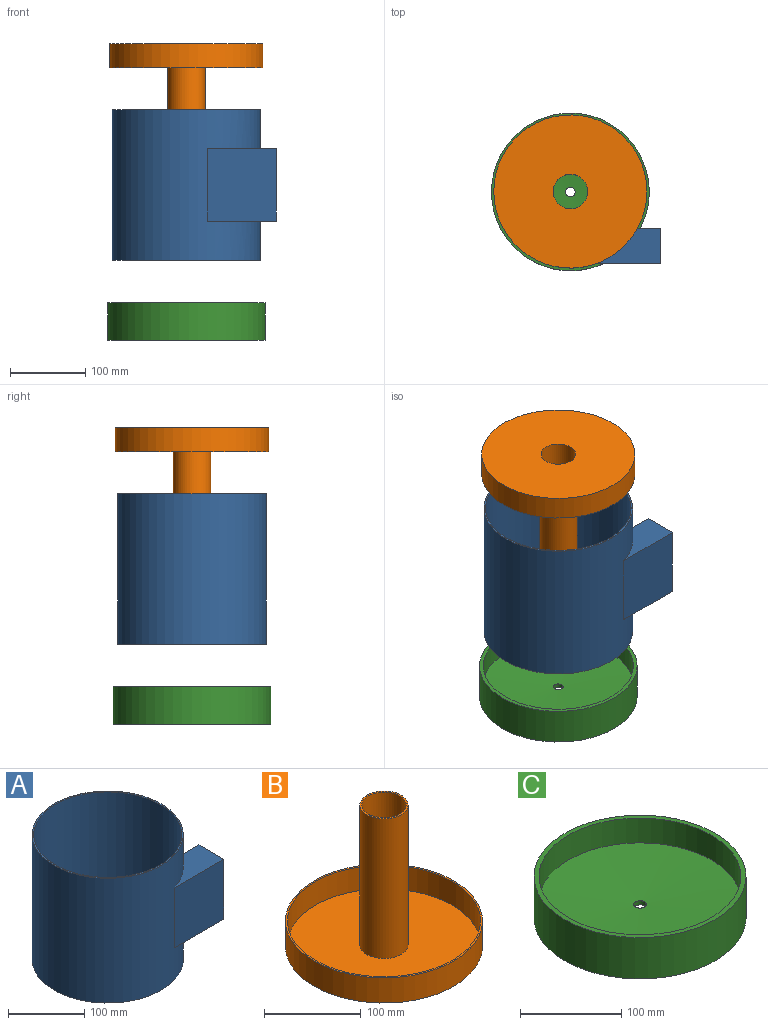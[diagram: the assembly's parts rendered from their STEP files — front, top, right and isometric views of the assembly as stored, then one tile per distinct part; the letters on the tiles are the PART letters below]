
ASSEMBLY  parts=3 mates=3
PART A: 9 faces, bbox 219x198x200 mm
  f0: cylinder r=99mm len=200mm, axis (0,0,-1), area 117110mm2, adj f2,f3,f4,f5,f6,f7
  f1: cylinder r=97mm len=200mm, axis (0,0,-1), area 121893.8mm2, adj f2,f3
  f2: plane 198x198mm, normal (0,0,-1), area 1231.5mm2, adj f0,f1
  f3: plane 198x198mm, normal (0,0,1), area 1231.5mm2, adj f0,f1
  f4: plane 96x92.14mm, normal (0,-1,0), area 8845.7mm2, adj f0,f5,f6,f8
  f5: plane 92.14x46mm, normal (0,0,1), area 2541.8mm2, adj f0,f4,f7,f8
  f6: plane 92.14x46mm, normal (0,0,-1), area 2541.8mm2, adj f0,f4,f7,f8
  f7: plane 96x33.98mm, normal (0,1,0), area 3261.8mm2, adj f0,f5,f6,f8
  f8: plane 96x46mm, normal (1,0,0), area 4416mm2, adj f4,f5,f6,f7
PART B: 8 faces, bbox 204x204x179 mm
  f0: cylinder r=102mm len=204mm, axis (0,0,-1), area 20508.3mm2, adj f1,f7
  f1: plane 204x204mm, normal (0,0,-1), area 31023.2mm2, adj f0,f2
  f2: cylinder r=23mm len=179mm, axis (0,0,-1), area 25867.9mm2, adj f1,f3
  f3: plane 50x50mm, normal (0,0,1), area 301.6mm2, adj f2,f4
  f4: cylinder r=25mm len=177mm, axis (0,0,-1), area 27803.1mm2, adj f3,f5
  f5: plane 200x200mm, normal (0,0,1), area 29452.4mm2, adj f4,f6
  f6: cylinder r=100mm len=200mm, axis (0,0,-1), area 18849.6mm2, adj f5,f7
  f7: plane 204x204mm, normal (0,0,1), area 1269.2mm2, adj f0,f6
PART C: 8 faces, bbox 210x210x50 mm
  f0: cylinder r=100mm len=200mm, axis (0,0,-1), area 9421.9mm2, adj f1,f7
  f1: cone r=6.35mm half-angle=87.6deg, axis (0,0,1), area 31317.8mm2, adj f0,f2
  f2: cylinder r=6.35mm len=12.7mm, axis (0,0,-1), area 199.7mm2, adj f1,f3
  f3: cone r=6.35mm half-angle=87.6deg, axis (0,0,1), area 31317.8mm2, adj f2,f4
  f4: cylinder r=100mm len=200mm, axis (0,0,-1), area 18849.6mm2, adj f3,f5
  f5: plane 210x210mm, normal (0,0,1), area 3220.1mm2, adj f4,f6
  f6: cylinder r=105mm len=210mm, axis (0,0,-1), area 32986.7mm2, adj f5,f7
  f7: plane 210x210mm, normal (0,0,-1), area 3220.1mm2, adj f0,f6
PLACE A rot(axis=(0,0,1),0deg) t=(-321.52,166.57,70.92)mm
PLACE B rot(axis=(1,0,0),180deg) t=(-321.52,166.57,357.14)mm
PLACE C rot(axis=(0,0,1),0deg) t=(-321.52,166.57,-16.05)mm
MATE slider A.f0 <-> B.f0  axis (0,0,1) through (-321.52,166.57,270.92)mm
MATE cylindrical B.f0 <-> C.f0  axis (0,0,1) through (-321.52,166.57,180.14)mm
MATE slider C.f0 <-> A.f0  axis (0,0,-1) through (-321.52,166.57,-16.05)mm
